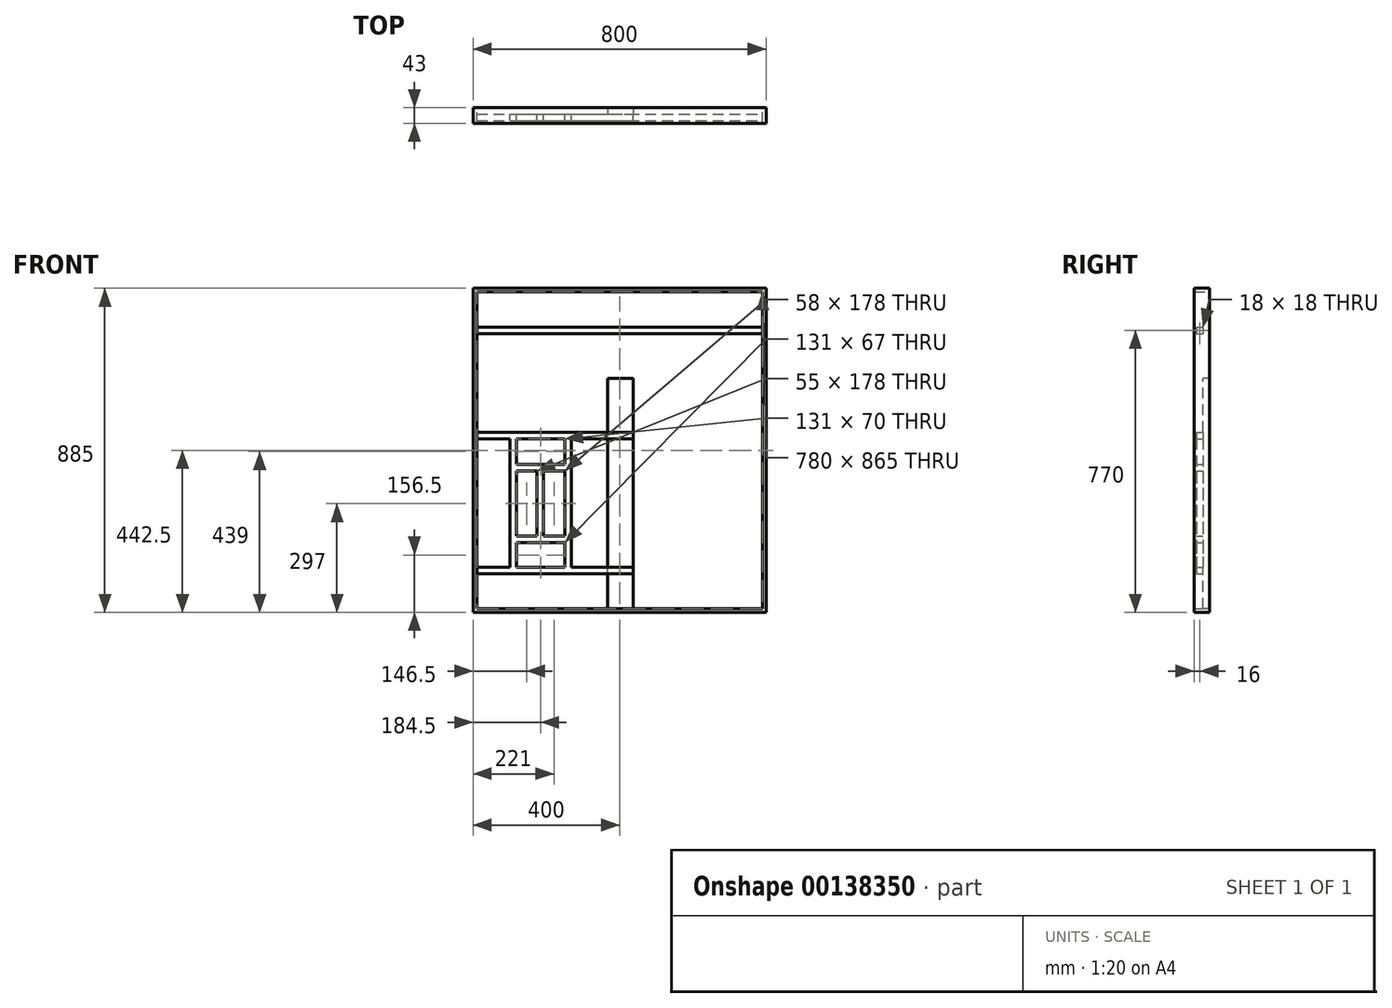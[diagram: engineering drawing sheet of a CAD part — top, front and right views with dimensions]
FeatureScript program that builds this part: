
annotation { "Feature Type Name" : "Feature", "Feature Type Description" : "" }
export const myFeature = defineFeature(function(context is Context, id is Id, definition is map)
    precondition{}
    {
        {
            var Q0;
            Q0=qCreatedBy(makeId("Front.planeOp"),FACE);
            var sketch = newSketch(context, id + "F0", { "sketchPlane" : qUnion([Q0])});
            skLineSegment(sketch, "E0.bottom", {"start": v(390, 432.5) * mm, "end": v(-390, 432.5) * mm});
            skLineSegment(sketch, "E0.top", {"start": v(390, -432.5) * mm, "end": v(-390, -432.5) * mm});
            skLineSegment(sketch, "E0.left", {"start": v(390, 432.5) * mm, "end": v(390, -432.5) * mm});
            skLineSegment(sketch, "E0.right", {"start": v(-390, 432.5) * mm, "end": v(-390, -432.5) * mm});
            skPoint(sketch, "E0.middle", {"position": v(0, 0) * mm});
            skLineSegment(sketch, "E1.bottom", {"start": v(-390, 336.5) * mm, "end": v(390, 336.5) * mm});
            skLineSegment(sketch, "E1.top", {"start": v(-390, 318.5) * mm, "end": v(390, 318.5) * mm});
            skLineSegment(sketch, "E1.left", {"start": v(-390, 336.5) * mm, "end": v(-390, 318.5) * mm});
            skLineSegment(sketch, "E1.right", {"start": v(390, 336.5) * mm, "end": v(390, 318.5) * mm});
            skLineSegment(sketch, "E2.bottom", {"start": v(-390, 49.5) * mm, "end": v(390, 49.5) * mm});
            skLineSegment(sketch, "E2.top", {"start": v(-390, 31.5) * mm, "end": v(-299, 31.5) * mm});
            skLineSegment(sketch, "E2.left", {"start": v(-390, 49.5) * mm, "end": v(-390, 31.5) * mm});
            skLineSegment(sketch, "E2.right", {"start": v(390, 49.5) * mm, "end": v(390, 31.5) * mm});
            skLineSegment(sketch, "E3.left", {"start": v(-390, -38.5) * mm, "end": v(-390, -56.5) * mm});
            skLineSegment(sketch, "E3.right", {"start": v(390, -38.5) * mm, "end": v(390, -56.5) * mm});
            skLineSegment(sketch, "E4.left", {"start": v(-390, 40.52) * mm, "end": v(-390, -140.5) * mm});
            skLineSegment(sketch, "E4.right", {"start": v(390, 40.52) * mm, "end": v(390, -252.5) * mm});
            skLineSegment(sketch, "E5.left", {"start": v(-390, -234.5) * mm, "end": v(-390, -252.5) * mm});
            skLineSegment(sketch, "E5.right", {"start": v(390, -234.5) * mm, "end": v(390, -252.5) * mm});
            skLineSegment(sketch, "E6.bottom", {"start": v(-390, -319.5) * mm, "end": v(-299, -319.5) * mm});
            skLineSegment(sketch, "E6.top", {"start": v(-390, -337.5) * mm, "end": v(390, -337.5) * mm});
            skLineSegment(sketch, "E6.left", {"start": v(-390, -319.5) * mm, "end": v(-390, -337.5) * mm});
            skLineSegment(sketch, "E6.right", {"start": v(390, -319.5) * mm, "end": v(390, -337.5) * mm});
            skLineSegment(sketch, "E7.bottom", {"start": v(301, 49.5) * mm, "end": v(283, 49.5) * mm});
            skLineSegment(sketch, "E7.top", {"start": v(301, -337.5) * mm, "end": v(283, -337.5) * mm});
            skLineSegment(sketch, "E7.left", {"start": v(301, 31.5) * mm, "end": v(301, -38.5) * mm});
            skLineSegment(sketch, "E7.right", {"start": v(283, 31.5) * mm, "end": v(283, -38.5) * mm});
            skLineSegment(sketch, "E8.bottom", {"start": v(151, 49.5) * mm, "end": v(133, 49.5) * mm});
            skLineSegment(sketch, "E8.top", {"start": v(151, -337.5) * mm, "end": v(133, -337.5) * mm});
            skLineSegment(sketch, "E8.left", {"start": v(151, 31.5) * mm, "end": v(151, -38.5) * mm});
            skLineSegment(sketch, "E8.right", {"start": v(133, 31.5) * mm, "end": v(133, -38.5) * mm});
            skLineSegment(sketch, "E9.bottom", {"start": v(224, -38.5) * mm, "end": v(206, -38.5) * mm});
            skLineSegment(sketch, "E9.top", {"start": v(224, -252.5) * mm, "end": v(206, -252.5) * mm});
            skLineSegment(sketch, "E9.left", {"start": v(224, -56.5) * mm, "end": v(224, -234.5) * mm});
            skLineSegment(sketch, "E9.right", {"start": v(206, -56.5) * mm, "end": v(206, -234.5) * mm});
            skLineSegment(sketch, "E10.bottom", {"start": v(-150, 49.5) * mm, "end": v(-132, 49.5) * mm});
            skLineSegment(sketch, "E10.top", {"start": v(-150, -337.5) * mm, "end": v(-132, -337.5) * mm});
            skLineSegment(sketch, "E10.left", {"start": v(-150, 31.5) * mm, "end": v(-150, -38.5) * mm});
            skLineSegment(sketch, "E10.right", {"start": v(-132, 31.5) * mm, "end": v(-132, -38.5) * mm});
            skLineSegment(sketch, "E11.bottom", {"start": v(-208, -38.5) * mm, "end": v(-226, -38.5) * mm});
            skLineSegment(sketch, "E11.top", {"start": v(-208, -252.5) * mm, "end": v(-226, -252.5) * mm});
            skLineSegment(sketch, "E11.left", {"start": v(-208, -56.5) * mm, "end": v(-208, -234.5) * mm});
            skLineSegment(sketch, "E11.right", {"start": v(-226, -56.5) * mm, "end": v(-226, -234.5) * mm});
            skLineSegment(sketch, "E12.bottom", {"start": v(-281, 49.5) * mm, "end": v(-299, 49.5) * mm});
            skLineSegment(sketch, "E12.top", {"start": v(-281, -337.5) * mm, "end": v(-299, -337.5) * mm});
            skLineSegment(sketch, "E12.left", {"start": v(-281, 31.5) * mm, "end": v(-281, -38.5) * mm});
            skLineSegment(sketch, "E12.right", {"start": v(-299, 31.5) * mm, "end": v(-299, -38.5) * mm});
            skLineSegment(sketch, "E13.bottom", {"start": v(-33, -432.5) * mm, "end": v(37, -432.5) * mm});
            skLineSegment(sketch, "E13.top", {"start": v(-33, 196.5) * mm, "end": v(37, 196.5) * mm});
            skLineSegment(sketch, "E13.left", {"start": v(-33, -432.5) * mm, "end": v(-33, 196.5) * mm});
            skLineSegment(sketch, "E13.right", {"start": v(37, -432.5) * mm, "end": v(37, 196.5) * mm});
            skLineSegment(sketch, "E14.bottom", {"start": v(-390, 196.5) * mm, "end": v(390, 196.5) * mm});
            skLineSegment(sketch, "E14.top", {"start": v(-390, 126.5) * mm, "end": v(390, 126.5) * mm});
            skLineSegment(sketch, "E14.left", {"start": v(-390, 196.5) * mm, "end": v(-390, 126.5) * mm});
            skLineSegment(sketch, "E14.right", {"start": v(390, 196.5) * mm, "end": v(390, 126.5) * mm});
            skLineSegment(sketch, "E15.trimOffspring", {"start": v(-208, -56.5) * mm, "end": v(-150, -56.5) * mm});
            skLineSegment(sketch, "E16.trimOffspring", {"start": v(-281, -56.5) * mm, "end": v(-281, -234.5) * mm});
            skLineSegment(sketch, "E17.trimOffspring", {"start": v(-150, -56.5) * mm, "end": v(-150, -234.5) * mm});
            skLineSegment(sketch, "E18.trimOffspring", {"start": v(-281, 31.5) * mm, "end": v(-150, 31.5) * mm});
            skLineSegment(sketch, "E19.trimOffspring", {"start": v(-132, 31.5) * mm, "end": v(133, 31.5) * mm});
            skLineSegment(sketch, "E20.trimOffspring", {"start": v(-208, -38.5) * mm, "end": v(-150, -38.5) * mm});
            skLineSegment(sketch, "E21.trimOffspring", {"start": v(-208, -234.5) * mm, "end": v(-150, -234.5) * mm});
            skLineSegment(sketch, "E22.trimOffspring", {"start": v(-281, -56.5) * mm, "end": v(-226, -56.5) * mm});
            skLineSegment(sketch, "E23.trimOffspring", {"start": v(-299, -56.5) * mm, "end": v(-299, -234.5) * mm});
            skLineSegment(sketch, "E24.trimOffspring", {"start": v(-281, -38.5) * mm, "end": v(-226, -38.5) * mm});
            skLineSegment(sketch, "E25.trimOffspring", {"start": v(-299, -252.5) * mm, "end": v(-299, -319.5) * mm});
            skLineSegment(sketch, "E26.trimOffspring", {"start": v(-281, -234.5) * mm, "end": v(-226, -234.5) * mm});
            skLineSegment(sketch, "E27.trimOffspring", {"start": v(-281, -252.5) * mm, "end": v(-281, -319.5) * mm});
            skLineSegment(sketch, "E28.trimOffspring", {"start": v(-281, -252.5) * mm, "end": v(-150, -252.5) * mm});
            skLineSegment(sketch, "E29.trimOffspring", {"start": v(-150, -252.5) * mm, "end": v(-150, -319.5) * mm});
            skLineSegment(sketch, "E30.trimOffspring", {"start": v(-132, -252.5) * mm, "end": v(-132, -319.5) * mm});
            skLineSegment(sketch, "E31.trimOffspring", {"start": v(-281, -319.5) * mm, "end": v(-150, -319.5) * mm});
            skLineSegment(sketch, "E32.trimOffspring", {"start": v(-132, -319.5) * mm, "end": v(133, -319.5) * mm});
            skLineSegment(sketch, "E33.trimOffspring", {"start": v(151, 31.5) * mm, "end": v(283, 31.5) * mm});
            skLineSegment(sketch, "E34.trimOffspring", {"start": v(301, 31.5) * mm, "end": v(390, 31.5) * mm});
            skLineSegment(sketch, "E35.trimOffspring", {"start": v(283, -56.5) * mm, "end": v(283, -234.5) * mm});
            skLineSegment(sketch, "E36.trimOffspring", {"start": v(301, -56.5) * mm, "end": v(301, -234.5) * mm});
            skLineSegment(sketch, "E37.trimOffspring", {"start": v(224, -56.5) * mm, "end": v(283, -56.5) * mm});
            skLineSegment(sketch, "E38.trimOffspring", {"start": v(133, -56.5) * mm, "end": v(133, -234.5) * mm});
            skLineSegment(sketch, "E39.trimOffspring", {"start": v(151, -38.5) * mm, "end": v(283, -38.5) * mm});
            skLineSegment(sketch, "E40.trimOffspring", {"start": v(151, -56.5) * mm, "end": v(151, -234.5) * mm});
            skLineSegment(sketch, "E41.trimOffspring", {"start": v(151, -56.5) * mm, "end": v(206, -56.5) * mm});
            skLineSegment(sketch, "E42.trimOffspring", {"start": v(224, -234.5) * mm, "end": v(283, -234.5) * mm});
            skLineSegment(sketch, "E43.trimOffspring", {"start": v(133, -252.5) * mm, "end": v(133, -319.5) * mm});
            skLineSegment(sketch, "E44.trimOffspring", {"start": v(151, -234.5) * mm, "end": v(206, -234.5) * mm});
            skLineSegment(sketch, "E45.trimOffspring", {"start": v(151, -319.5) * mm, "end": v(283, -319.5) * mm});
            skLineSegment(sketch, "E46.trimOffspring", {"start": v(301, -319.5) * mm, "end": v(390, -319.5) * mm});
            skLineSegment(sketch, "E47.trimOffspring", {"start": v(283, -252.5) * mm, "end": v(283, -319.5) * mm});
            skLineSegment(sketch, "E48.trimOffspring", {"start": v(301, -252.5) * mm, "end": v(301, -319.5) * mm});
            skLineSegment(sketch, "E49.trimOffspring", {"start": v(151, -252.5) * mm, "end": v(151, -319.5) * mm});
            skLineSegment(sketch, "E50.trimOffspring", {"start": v(-132, -56.5) * mm, "end": v(-132, -234.5) * mm});
            skLineSegment(sketch, "E51.bottom", {"start": v(-400, 442.5) * mm, "end": v(400, 442.5) * mm});
            skLineSegment(sketch, "E51.top", {"start": v(-400, -442.5) * mm, "end": v(400, -442.5) * mm});
            skLineSegment(sketch, "E51.left", {"start": v(-400, 442.5) * mm, "end": v(-400, -442.5) * mm});
            skLineSegment(sketch, "E51.right", {"start": v(400, 442.5) * mm, "end": v(400, -442.5) * mm});
            skLineSegment(sketch, "E52", {"start": v(-299, -38.5) * mm, "end": v(-299, -56.5) * mm});
            skLineSegment(sketch, "E53", {"start": v(-299, -234.5) * mm, "end": v(-299, -252.5) * mm});
            skLineSegment(sketch, "E54", {"start": v(301, -38.5) * mm, "end": v(301, -56.5) * mm});
            skLineSegment(sketch, "E55", {"start": v(301, -234.5) * mm, "end": v(301, -252.5) * mm});
            skLineSegment(sketch, "E56", {"start": v(133, -38.5) * mm, "end": v(133, -56.5) * mm});
            skLineSegment(sketch, "E57", {"start": v(133, -234.5) * mm, "end": v(133, -252.5) * mm});
            skLineSegment(sketch, "E58", {"start": v(-132, -234.5) * mm, "end": v(-132, -252.5) * mm});
            skLineSegment(sketch, "E59", {"start": v(-132, -56.5) * mm, "end": v(-132, -38.5) * mm});
            skLineSegment(sketch, "E60.trimOffspring", {"start": v(151, -252.5) * mm, "end": v(283, -252.5) * mm});
            skSolve(sketch);
        }
        {
            var Q0;
            {var subQ20=sQuery(id+"F0.wireOp",EDGE,"E2.top");Q0=makeQuery(id+"F0.imprint","IMPRINT",FACE,{"disambiguationData":[TD([[makeQuery(id+"F0.imprint","IMPRINT",EDGE,{"derivedFrom":subQ20}),1.0]])]});}
            var Q1;
            {var subQ23=sQuery(id+"F0.wireOp",EDGE,"E2.right");Q1=makeQuery(id+"F0.imprint","IMPRINT",FACE,{"disambiguationData":[TD([[makeQuery(id+"F0.imprint","IMPRINT",EDGE,{"derivedFrom":subQ23}),-1.0]])]});}
            var Q2;
            {var subQ0=sQuery(id+"F0.wireOp",EDGE,"E13.left");var subQ1=sQuery(id+"F0.wireOp",EDGE,"E2.bottom");var subQ2=makeQuery(id+"F0.imprint","INTERSECT",VERTEX,{"derivedFrom":[subQ1,subQ0]});Q2=makeQuery(id+"F0.imprint","IMPRINT",FACE,{"disambiguationData":[TD([[makeQuery(id+"F0.imprint","IMPRINT",EDGE,{"disambiguationData":[TD([[subQ2,-1.0]])],"derivedFrom":subQ1}),-1.0]])]});}
            var Q3;
            {var subQ0=sQuery(id+"F0.wireOp",EDGE,"E13.left");var subQ1=sQuery(id+"F0.wireOp",EDGE,"E6.top");var subQ2=makeQuery(id+"F0.imprint","INTERSECT",VERTEX,{"derivedFrom":[subQ1,subQ0]});Q3=makeQuery(id+"F0.imprint","IMPRINT",FACE,{"disambiguationData":[TD([[makeQuery(id+"F0.imprint","IMPRINT",EDGE,{"disambiguationData":[TD([[subQ2,-1.0]])],"derivedFrom":subQ1}),1.0]])]});}
            var Q4;
            Q4=makeQuery(id+"F0.imprint","IMPRINT",FACE,{"disambiguationData":[TD([[makeQuery(id+"F0.imprint","IMPRINT",EDGE,{"derivedFrom":sQuery(id+"F0.wireOp",EDGE,"E1.bottom")}),-1.0]])]});
            extrude(context, id + "F1", {"entities" : qUnion([Q0, Q1, Q2, Q3, Q4]), "depth" : 18 * mm});
        }
        {
            var Q0;
            Q0 = qSketchRegion(id + "F0", true);
            extrude(context, id + "F2", {"entities" : qUnion([Q0]), "operationType" : NewBodyOperationType.ADD, "depth" : 25 * mm});
        }
        {
            var Q0;
            {var subQ5=sQuery(id+"F0.wireOp",EDGE,"E14.right");Q0=makeQuery(id+"F0.imprint","IMPRINT",FACE,{"disambiguationData":[TD([[makeQuery(id+"F0.imprint","IMPRINT",EDGE,{"derivedFrom":subQ5}),-1.0]])]});}
            var Q1;
            {var subQ5=sQuery(id+"F0.wireOp",EDGE,"E14.left");Q1=makeQuery(id+"F0.imprint","IMPRINT",FACE,{"disambiguationData":[TD([[makeQuery(id+"F0.imprint","IMPRINT",EDGE,{"derivedFrom":subQ5}),1.0]])]});}
            var Q2;
            {var subQ0=sQuery(id+"F0.wireOp",EDGE,"E14.bottom");var subQ1=sQuery(id+"F0.wireOp",EDGE,"E13.left");var subQ2=makeQuery(id+"F0.imprint","INTERSECT",VERTEX,{"derivedFrom":[subQ1,subQ0]});Q2=makeQuery(id+"F0.imprint","IMPRINT",FACE,{"disambiguationData":[TD([[makeQuery(id+"F0.imprint","IMPRINT",EDGE,{"disambiguationData":[TD([[subQ2,1.0]])],"derivedFrom":subQ1}),-1.0]])]});}
            var Q3;
            {var subQ0=sQuery(id+"F0.wireOp",EDGE,"E13.left");var subQ1=sQuery(id+"F0.wireOp",EDGE,"E2.bottom");var subQ2=makeQuery(id+"F0.imprint","INTERSECT",VERTEX,{"derivedFrom":[subQ1,subQ0]});Q3=makeQuery(id+"F0.imprint","IMPRINT",FACE,{"disambiguationData":[TD([[makeQuery(id+"F0.imprint","IMPRINT",EDGE,{"disambiguationData":[TD([[subQ2,-1.0]])],"derivedFrom":subQ1}),1.0]])]});}
            var Q4;
            {var subQ0=sQuery(id+"F0.wireOp",EDGE,"E13.left");var subQ1=sQuery(id+"F0.wireOp",EDGE,"E2.bottom");var subQ2=makeQuery(id+"F0.imprint","INTERSECT",VERTEX,{"derivedFrom":[subQ1,subQ0]});Q4=makeQuery(id+"F0.imprint","IMPRINT",FACE,{"disambiguationData":[TD([[makeQuery(id+"F0.imprint","IMPRINT",EDGE,{"disambiguationData":[TD([[subQ2,-1.0]])],"derivedFrom":subQ1}),-1.0]])]});}
            var Q5;
            {var subQ0=sQuery(id+"F0.wireOp",EDGE,"f4ab771c-46ae-412c-b049-d0a5c875f43f.trimOffspring");var subQ1=sQuery(id+"F0.wireOp",EDGE,"E13.left");var subQ2=makeQuery(id+"F0.imprint","INTERSECT",VERTEX,{"derivedFrom":[subQ1,subQ0]});Q5=makeQuery(id+"F0.imprint","IMPRINT",FACE,{"disambiguationData":[TD([[makeQuery(id+"F0.imprint","IMPRINT",EDGE,{"disambiguationData":[TD([[subQ2,-1.0]])],"derivedFrom":subQ1}),-1.0]])]});}
            var Q6;
            {var subQ0=sQuery(id+"F0.wireOp",EDGE,"cbe895b8-37ec-48ef-9d72-b73097176d58.trimOffspring");var subQ1=sQuery(id+"F0.wireOp",EDGE,"E13.left");var subQ2=makeQuery(id+"F0.imprint","INTERSECT",VERTEX,{"derivedFrom":[subQ1,subQ0]});Q6=makeQuery(id+"F0.imprint","IMPRINT",FACE,{"disambiguationData":[TD([[makeQuery(id+"F0.imprint","IMPRINT",EDGE,{"disambiguationData":[TD([[subQ2,-1.0]])],"derivedFrom":subQ1}),-1.0]])]});}
            var Q7;
            {var subQ0=sQuery(id+"F0.wireOp",EDGE,"23ffac06-726c-4705-a3e8-f697eddd4ea4.trimOffspring");var subQ1=sQuery(id+"F0.wireOp",EDGE,"E13.left");var subQ2=makeQuery(id+"F0.imprint","INTERSECT",VERTEX,{"derivedFrom":[subQ1,subQ0]});Q7=makeQuery(id+"F0.imprint","IMPRINT",FACE,{"disambiguationData":[TD([[makeQuery(id+"F0.imprint","IMPRINT",EDGE,{"disambiguationData":[TD([[subQ2,-1.0]])],"derivedFrom":subQ1}),-1.0]])]});}
            var Q8;
            {var subQ0=sQuery(id+"F0.wireOp",EDGE,"db442b11-98cc-4cfe-903e-0cb9323f97a3.trimOffspring");var subQ1=sQuery(id+"F0.wireOp",EDGE,"E13.left");var subQ2=makeQuery(id+"F0.imprint","INTERSECT",VERTEX,{"derivedFrom":[subQ1,subQ0]});Q8=makeQuery(id+"F0.imprint","IMPRINT",FACE,{"disambiguationData":[TD([[makeQuery(id+"F0.imprint","IMPRINT",EDGE,{"disambiguationData":[TD([[subQ2,-1.0]])],"derivedFrom":subQ1}),-1.0]])]});}
            var Q9;
            {var subQ0=sQuery(id+"F0.wireOp",EDGE,"E32.trimOffspring");var subQ1=sQuery(id+"F0.wireOp",EDGE,"E13.left");var subQ2=makeQuery(id+"F0.imprint","INTERSECT",VERTEX,{"derivedFrom":[subQ1,subQ0]});Q9=makeQuery(id+"F0.imprint","IMPRINT",FACE,{"disambiguationData":[TD([[makeQuery(id+"F0.imprint","IMPRINT",EDGE,{"disambiguationData":[TD([[subQ2,-1.0]])],"derivedFrom":subQ1}),-1.0]])]});}
            var Q10;
            {var subQ0=sQuery(id+"F0.wireOp",EDGE,"E13.left");var subQ1=sQuery(id+"F0.wireOp",EDGE,"E6.top");var subQ2=makeQuery(id+"F0.imprint","INTERSECT",VERTEX,{"derivedFrom":[subQ1,subQ0]});Q10=makeQuery(id+"F0.imprint","IMPRINT",FACE,{"disambiguationData":[TD([[makeQuery(id+"F0.imprint","IMPRINT",EDGE,{"disambiguationData":[TD([[subQ2,-1.0]])],"derivedFrom":subQ1}),1.0]])]});}
            var Q11;
            {var subQ5=sQuery(id+"F0.wireOp",EDGE,"E13.bottom");Q11=makeQuery(id+"F0.imprint","IMPRINT",FACE,{"disambiguationData":[TD([[makeQuery(id+"F0.imprint","IMPRINT",EDGE,{"derivedFrom":subQ5}),1.0]])]});}
            var Q12;
            {var subQ24=sQuery(id+"F0.wireOp",EDGE,"E0.bottom");Q12=makeQuery(id+"F0.imprint","IMPRINT",FACE,{"disambiguationData":[TD([[makeQuery(id+"F0.imprint","IMPRINT",EDGE,{"derivedFrom":subQ24}),-1.0]])]});}
            extrude(context, id + "F3", {"entities" : qUnion([Q0, Q1, Q2, Q3, Q4, Q5, Q6, Q7, Q8, Q9, Q10, Q11, Q12]), "operationType" : NewBodyOperationType.ADD, "oppositeDirection" : true, "depth" : 18 * mm});
        }
    });
